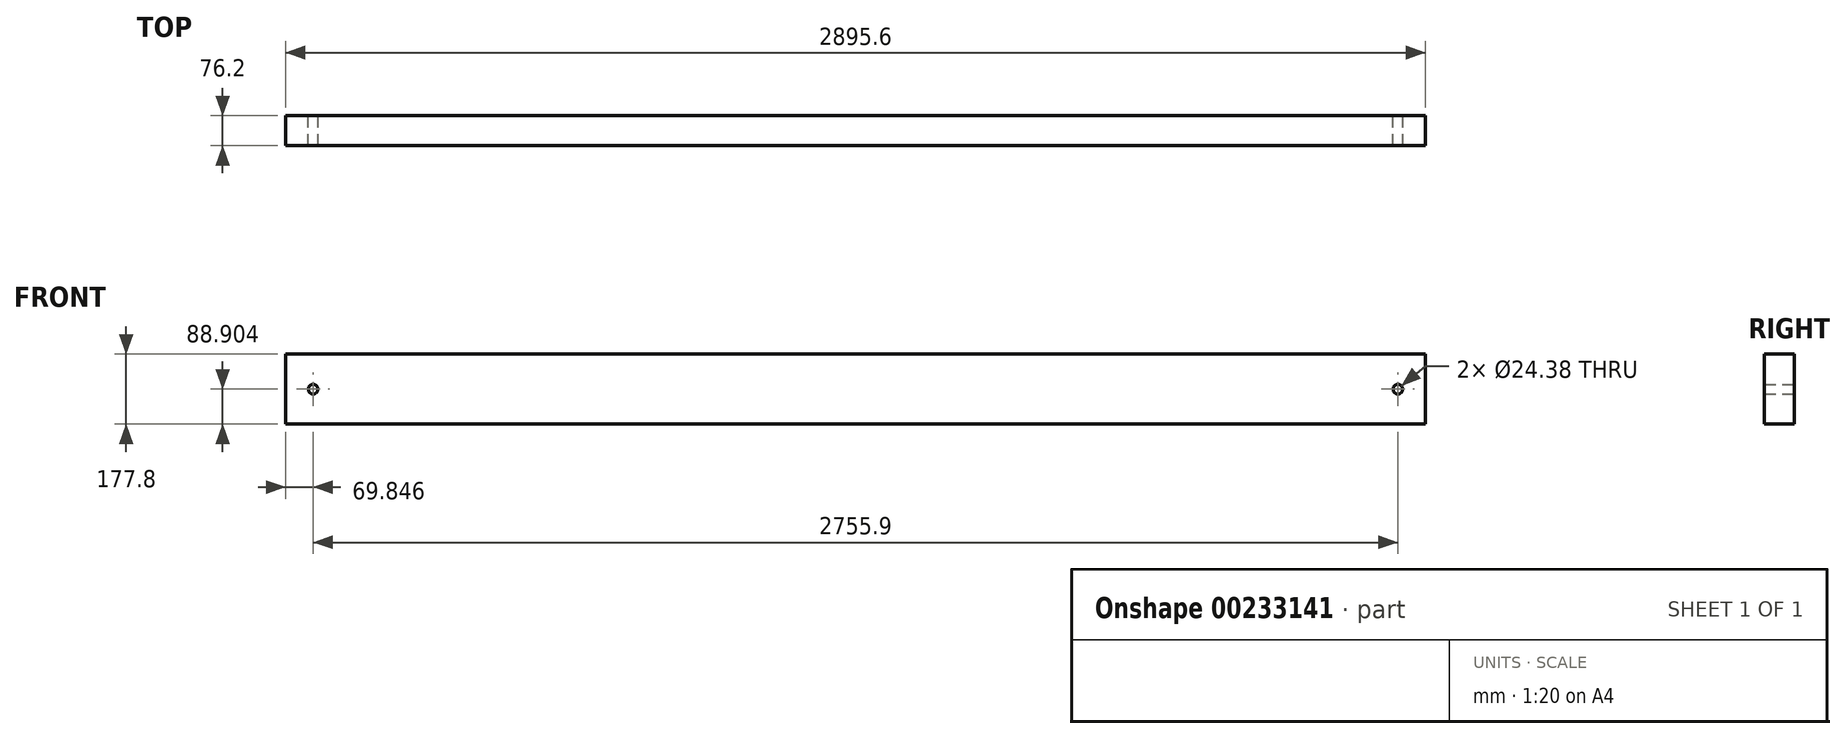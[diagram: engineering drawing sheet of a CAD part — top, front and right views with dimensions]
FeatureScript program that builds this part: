
annotation { "Feature Type Name" : "Feature", "Feature Type Description" : "" }
export const myFeature = defineFeature(function(context is Context, id is Id, definition is map)
    precondition{}
    {
        {
            var Q0;
            Q0=qCreatedBy(makeId("Front.planeOp"),FACE);
            var sketch = newSketch(context, id + "F0", { "sketchPlane" : qUnion([Q0])});
            skLineSegment(sketch, "E0.bottom", {"start": v(-1368.72, -236.94) * mm, "end": v(1526.88, -236.94) * mm});
            skLineSegment(sketch, "E0.top", {"start": v(-1368.72, -414.74) * mm, "end": v(1526.88, -414.74) * mm});
            skLineSegment(sketch, "E0.left", {"start": v(-1368.72, -236.94) * mm, "end": v(-1368.72, -414.74) * mm});
            skLineSegment(sketch, "E0.right", {"start": v(1526.88, -236.94) * mm, "end": v(1526.88, -414.74) * mm});
            skCircle(sketch, "E1", {"center": v(-1298.87, -325.84) * mm, "radius": 12.2 * mm});
            skPoint(sketch, "E1.centerSnap0", {"position": v(-1368.72, -325.84) * mm});
            skCircle(sketch, "E2", {"center": v(1457.03, -325.84) * mm, "radius": 12.2 * mm});
            skSolve(sketch);
        }
        {
            var Q0;
            Q0 = qSketchRegion(id + "F0", true);
            extrude(context, id + "F1", {"entities" : qUnion([Q0]), "depth" : 76.2 * mm});
        }
    });
